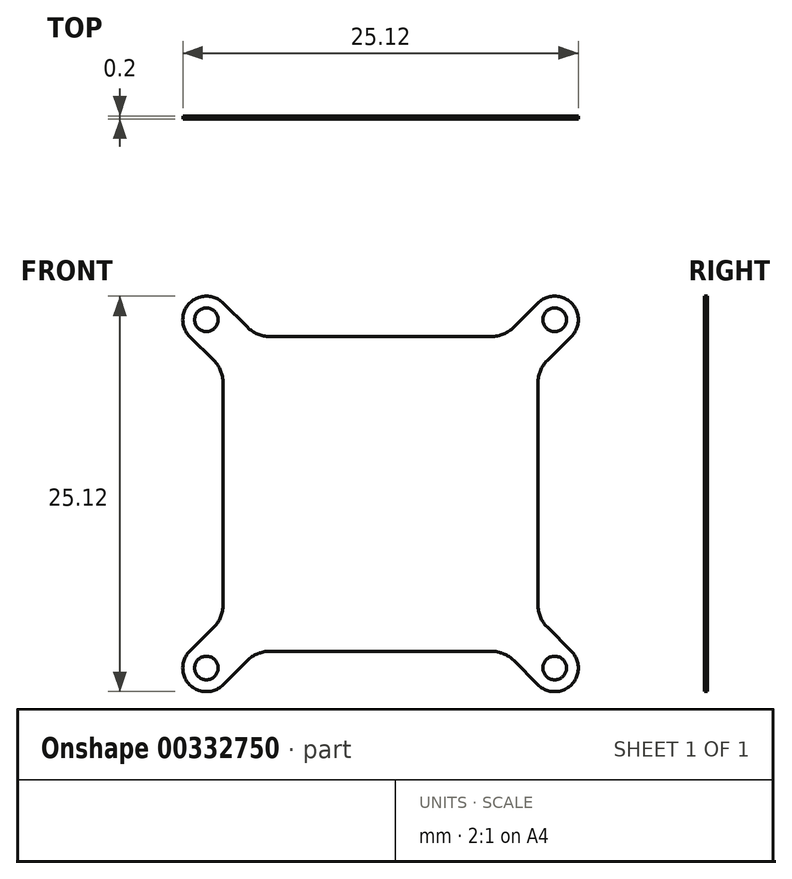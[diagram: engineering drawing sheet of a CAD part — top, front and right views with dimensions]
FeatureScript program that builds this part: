
annotation { "Feature Type Name" : "Feature", "Feature Type Description" : "" }
export const myFeature = defineFeature(function(context is Context, id is Id, definition is map)
    precondition{}
    {
        {
            var Q0;
            Q0=qCreatedBy(makeId("Front.planeOp"),FACE);
            var sketch = newSketch(context, id + "F0", { "sketchPlane" : qUnion([Q0])});
            skLineSegment(sketch, "E0.bottom", {"start": v(0, 10) * mm, "end": v(-7.05, 10) * mm});
            skLineSegment(sketch, "E0.top", {"start": v(10, -10) * mm, "end": v(-10, -10) * mm});
            skLineSegment(sketch, "E0.left", {"start": v(10, 10) * mm, "end": v(10, -10) * mm});
            skLineSegment(sketch, "E0.right", {"start": v(-10, 7.05) * mm, "end": v(-10, 0) * mm});
            skPoint(sketch, "E0.middle", {"position": v(0, 0) * mm});
            skArc(sketch, "E1", {"start": v(-10, 12.12) * mm, "mid": v(-12.12, 12.12) * mm, "end": v(-12.12, 10) * mm});
            skLineSegment(sketch, "E2", {"start": v(0, 0) * mm, "end": v(-11.06, 11.06) * mm, "construction": true});
            skLineSegment(sketch, "E3", {"start": v(-10.59, 8.46) * mm, "end": v(-12.12, 10) * mm});
            skLineSegment(sketch, "E4", {"start": v(-10, 12.12) * mm, "end": v(-8.46, 10.59) * mm});
            skArc(sketch, "E5.filletArc", {"start": v(-10, 7.05) * mm, "mid": v(-10.15, 7.82) * mm, "end": v(-10.59, 8.46) * mm});
            skPoint(sketch, "E6.newPointB", {"position": v(-10, 10) * mm});
            skArc(sketch, "E6.filletArc", {"start": v(-8.46, 10.59) * mm, "mid": v(-7.82, 10.15) * mm, "end": v(-7.05, 10) * mm});
            skCircle(sketch, "E7", {"center": v(-11.06, 11.06) * mm, "radius": 0.75 * mm, "construction": true});
            skLineSegment(sketch, "E8", {"start": v(0, 0) * mm, "end": v(0, 10) * mm});
            skLineSegment(sketch, "E9", {"start": v(0, 0) * mm, "end": v(-10, 0) * mm});
            skSolve(sketch);
        }
        {
            var Q0;
            Q0=makeQuery(id+"F0.imprint","IMPRINT",FACE,{"disambiguationData":[TD([[makeQuery(id+"F0.imprint","IMPRINT",EDGE,{"derivedFrom":sQuery(id+"F0.wireOp",EDGE,"E0.bottom")}),1.0]])]});
            extrude(context, id + "F1", {"entities" : qUnion([Q0]), "depth" : 0.2 * mm});
        }
        {
            var Q0;
            Q0=makeQuery(id+"F1.opExtrude","SWEPT_BODY",BODY,{"disambiguationData":[OSD([sQuery(id+"F0.wireOp",EDGE,"E0.bottom"),sQuery(id+"F0.wireOp",EDGE,"E0.right"),sQuery(id+"F0.wireOp",EDGE,"E1"),sQuery(id+"F0.wireOp",EDGE,"E3"),sQuery(id+"F0.wireOp",EDGE,"E4"),sQuery(id+"F0.wireOp",EDGE,"E5.filletArc"),sQuery(id+"F0.wireOp",EDGE,"E6.filletArc"),sQuery(id+"F0.wireOp",EDGE,"E8"),sQuery(id+"F0.wireOp",EDGE,"E9")])]});
            var Q1;
            Q1=makeQuery(id+"F1.opExtrude","SWEPT_EDGE",EDGE,{"disambiguationData":[OSD([sQuery(id+"F0.wireOp",EDGE,"E8"),sQuery(id+"F0.wireOp",EDGE,"E9")])]});
            circularPattern(context, id + "F2", {"operationType" : NewBodyOperationType.ADD, "entities" : qUnion([Q0]), "axis" : qUnion([Q1]), "angle" : 360 * degree, "instanceCount" : 4, "equalSpace" : true});
        }
        {
            var Q0;
            Q0=qCreatedBy(makeId("Front.planeOp"),FACE);
            var sketch = newSketch(context, id + "F3", { "sketchPlane" : qUnion([Q0])});
            skArc(sketch, "E10.0", {"start": v(-10, 12.12) * mm, "mid": v(-12.12, 12.12) * mm, "end": v(-12.12, 10) * mm, "construction": true});
            skPoint(sketch, "E10.1", {"position": v(0, 0) * mm});
            skCircle(sketch, "E11", {"center": v(-11.06, 11.06) * mm, "radius": 0.75 * mm, "construction": true});
            skCircle(sketch, "E12.1.0", {"center": v(-11.06, -11.06) * mm, "radius": 0.75 * mm});
            skCircle(sketch, "E12.2.0", {"center": v(11.06, -11.06) * mm, "radius": 0.75 * mm});
            skCircle(sketch, "E12.3.0", {"center": v(11.06, 11.06) * mm, "radius": 0.75 * mm});
            skCircle(sketch, "E13", {"center": v(-11.06, 11.06) * mm, "radius": 0.75 * mm});
            skSolve(sketch);
        }
        {
            var Q0;
            Q0 = qSketchRegion(id + "F3", true);
            var Q1;
            {var subQ0=makeQuery(id+"F1.opExtrude","CAP_FACE",FACE,{"disambiguationData":[OSD([sQuery(id+"F0.wireOp",EDGE,"E0.bottom"),sQuery(id+"F0.wireOp",EDGE,"E0.right"),sQuery(id+"F0.wireOp",EDGE,"E1"),sQuery(id+"F0.wireOp",EDGE,"E3"),sQuery(id+"F0.wireOp",EDGE,"E4"),sQuery(id+"F0.wireOp",EDGE,"E5.filletArc"),sQuery(id+"F0.wireOp",EDGE,"E6.filletArc"),sQuery(id+"F0.wireOp",EDGE,"E8"),sQuery(id+"F0.wireOp",EDGE,"E9")])],"isStart":false});Q1=makeQuery(id+"F2.boolean.opBoolean","MERGE",FACE,{"derivedFrom":[subQ0,makeQuery(id+"F2.opPattern","COPY",FACE,{"derivedFrom":subQ0,"instanceName":"1"}),makeQuery(id+"F2.opPattern","COPY",FACE,{"derivedFrom":subQ0,"instanceName":"2"}),makeQuery(id+"F2.opPattern","COPY",FACE,{"derivedFrom":subQ0,"instanceName":"3"})]});}
            extrude(context, id + "F4", {"entities" : qUnion([Q0]), "endBound" : BoundingType.UP_TO_SURFACE, "endBoundEntityFace" : qUnion([Q1]), "depth" : 25 * mm});
        }
    });
